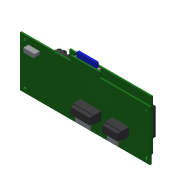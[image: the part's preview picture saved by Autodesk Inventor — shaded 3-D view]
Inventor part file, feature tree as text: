
AUTODESK INVENTOR PART (.ipt)
format: ipt  version: 2016 (Build 200138000, 138)  size: 692,224 bytes
history: native  units: mm
features: extrude x17, sketch x17, fillet x4, projected_geometry x2, plane x1, chamfer x1, pattern_circular x1, other x1
ambient origin geometry x8: Origin, YZ Plane, XZ Plane, XY Plane, X Axis, Y Axis, Z Axis, Center Point
bodies: Solid1 (feature_tree), Solid2 (feature_tree), Solid3 (feature_tree), Solid4 (feature_tree), Solid5 (feature_tree), Solid6 (feature_tree), Solid7 (feature_tree), Solid8 (feature_tree)
feature tree (44):
  extrude  "Extrusion1"  Depth=60.0mm
  plane  "Work Plane1"
  extrude  "Extrusion2"  Depth=6.0mm
  extrude  "Extrusion3"  Depth=60.0mm
  extrude  "Extrusion4"  Depth=5.0mm
  extrude  "Extrusion5"  Depth=3.2mm
  extrude  "Extrusion6"  Depth=5.0mm
  chamfer  "Chamfer1"  Distance=5.0mm
  fillet  "Fillet1"  Radius=5.0mm
  extrude  "Extrusion7"  Depth=5.0mm
  pattern_circular  "Circular Pattern1"  Count=3  [1 undecoded]
  fillet  "Fillet2"  Radius=30.0mm
  sketch  "Sketch8"  dims[d19=5.0mm]
  extrude  "Extrusion8"  Depth=17.0mm TaperAngle=0.0deg
  extrude  "Extrusion9"  Depth=10.0mm TaperAngle=0.0deg
  extrude  "Extrusion10"  Depth=28.5mm
  extrude  "Extrusion11"  Depth=10.0mm
  extrude  "Extrusion12"  Depth=10.0mm
  fillet  "Fillet3"  Radius=3.0mm
  extrude  "Extrusion13"  Depth=10.0mm TaperAngle=45.0deg
  fillet  "Fillet4"  Radius=6.0mm
  extrude  "Extrusion14"  TaperAngle=0.0deg  [1 undecoded]
  extrude  "Extrusion15"  Depth=10.0mm TaperAngle=360.0deg
  extrude  "Extrusion16"  Depth=3.0mm
  extrude  "Extrusion17"  Depth=10.0mm
  sketch  "Sketch1"  dims[d0=155.0mm d1=60.0mm]
  sketch  "Sketch2"  dims[d2=1.8mm d3=0.0mm d4=6.0mm]
  sketch  "Sketch3"  dims[d5=35.0mm d6=60.0mm]
  sketch  "Sketch4"  dims[d7=3.2mm d8=5.0mm d9=5.0mm]
  sketch  "Sketch5"  dims[d10=3.2mm d11=3.2mm]
  sketch  "Sketch6"  dims[d12=3.2mm d13=5.0mm d14=5.0mm d15=5.0mm d16=5.0mm]
  sketch  "Sketch7"  dims[d17=5.0mm d18=5.0mm]
  sketch  "Sketch9"  dims[d20=5.0mm]
  sketch  "Sketch10"  dims[d21=10.0mm]
  sketch  "Sketch11"  dims[d23=98.0mm]
  sketch  "Sketch12"  dims[d24=1.8mm d25=0.0mm]
  sketch  "Sketch13"  dims[d26=13.0mm]
  sketch  "Sketch15"  dims[d27=12.5mm]
  sketch  "Sketch16"  dims[d28=6.0mm d29=0.0mm d30=30.0mm d31=30.0mm]
  projected_geometry  "Projected Loop2"
  sketch  "Sketch17"  dims[d32=6.0mm d33=17.0mm d34=0.0mm]
  projected_geometry  "Projected Loop3"
  sketch  "Sketch18"  dims[d35=30.0mm d36=8.5mm d37=0.0mm d38=28.5mm d39=30.0mm d40=3.25mm d41=3.0mm d42=0.0mm d43=4.0mm d44=2.0mm d45=45.0deg d46=6.0mm d47=0.0mm d48=0.0mm d49=140.0mm d50=360.0deg d52=3.0mm d53=24.0mm d54=2.5mm d55=2.25mm d56=6.0mm d57=0.0mm d58=94.0mm d59=32.0mm d60=2.0mm d61=5.0mm d62=0.0mm d63=77.0mm d64=25.0mm d65=8.5mm d66=0.5mm d67=0.0mm d68=1.0mm d69=0.0mm d70=10.0mm d71=0.0mm d72=20.0mm d73=2.5mm d74=0.0mm d75=1.0mm d76=3.0mm d77=3.0mm d78=3.0mm d79=1.0mm d80=0.1mm d81=4.0mm d82=0.1mm d83=0.0mm d84=4.0mm d85=1.0mm d86=1.0mm d92=17.0mm d93=10.0mm d95=17.0mm d96=10.0mm d97=20.0mm d98=25.0mm d99=13.0mm d100=0.0mm d101=10.2mm d102=10.2mm d103=1.4mm d104=1.4mm d105=4.0mm d106=4.0mm d107=4.0mm d108=4.0mm d109=13.0mm d110=0.0mm d111=1.0mm d112=1.0mm d113=13.0mm d114=0.0mm d115=25.0mm d116=83.0mm d117=1.5mm d118=5.0mm d119=13.5mm d120=135.0deg d121=8.0mm d122=10.0mm d138=6.0mm d139=0.0mm]
  other  "Image1"
note: 2 required parameter values undecoded (feature->parameter linkage not recoverable at this tier; creation-order binding heuristic only, values carry confidence <= 0.55)
